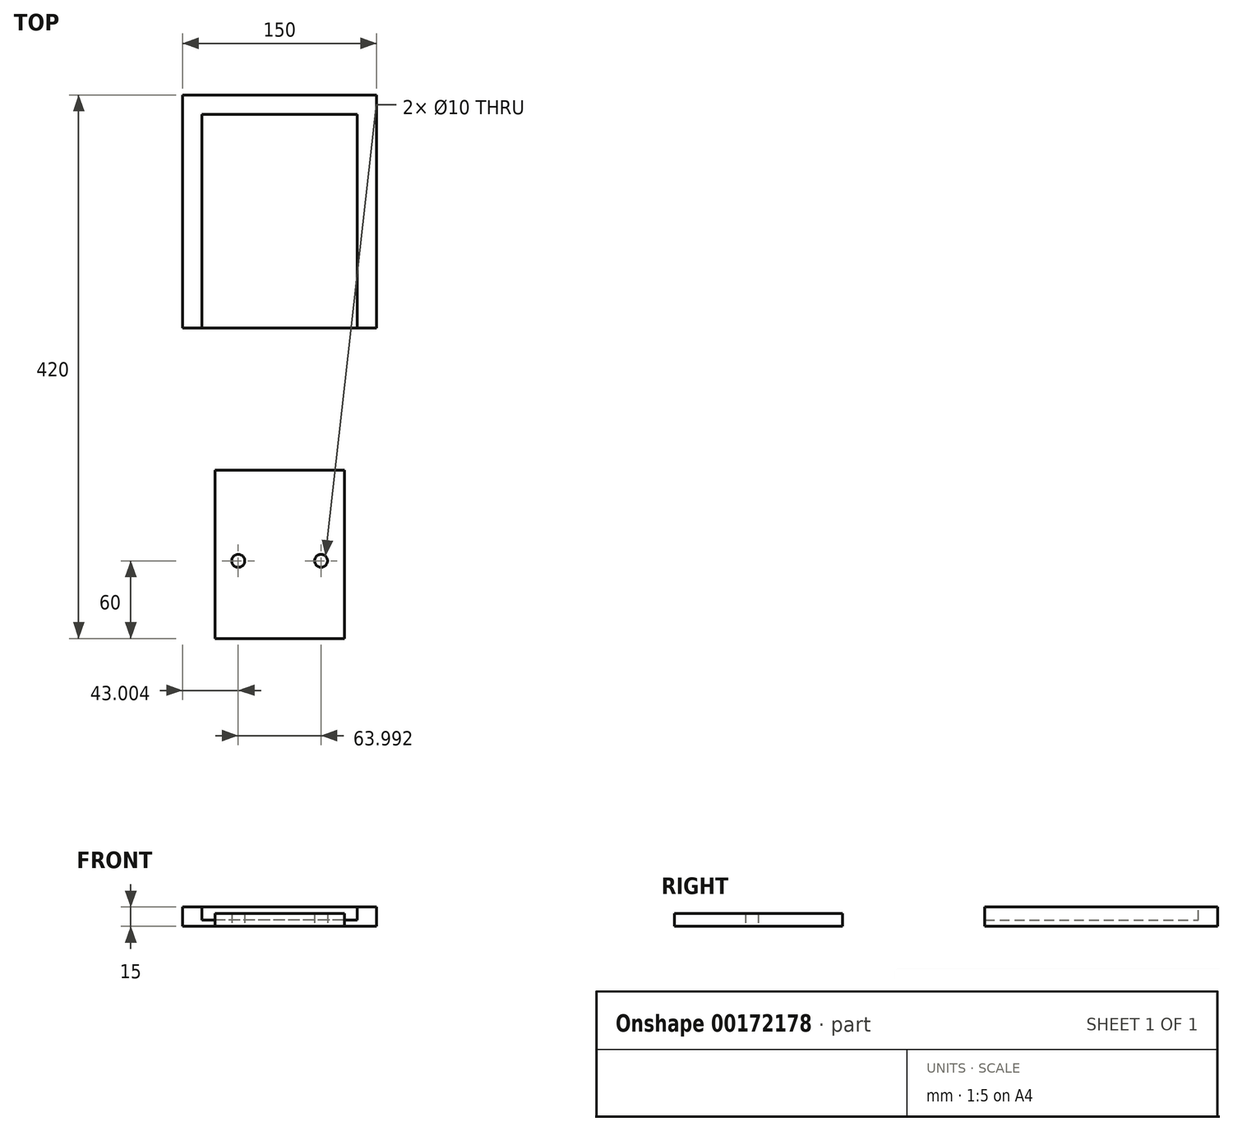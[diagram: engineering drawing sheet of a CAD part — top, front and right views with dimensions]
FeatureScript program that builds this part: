
annotation { "Feature Type Name" : "Feature", "Feature Type Description" : "" }
export const myFeature = defineFeature(function(context is Context, id is Id, definition is map)
    precondition{}
    {
        {
            var Q0;
            Q0=qCreatedBy(makeId("Top.planeOp"),FACE);
            var sketch = newSketch(context, id + "F0", { "sketchPlane" : qUnion([Q0])});
            skLineSegment(sketch, "E0.bottom", {"start": v(50, -90) * mm, "end": v(-50, -90) * mm});
            skLineSegment(sketch, "E0.top", {"start": v(50, 40) * mm, "end": v(-50, 40) * mm});
            skLineSegment(sketch, "E0.left", {"start": v(50, -90) * mm, "end": v(50, 40) * mm});
            skLineSegment(sketch, "E0.right", {"start": v(-50, -90) * mm, "end": v(-50, 40) * mm});
            skPoint(sketch, "E0.middle", {"position": v(0, -25) * mm});
            skSolve(sketch);
        }
        {
            var Q0;
            Q0 = qSketchRegion(id + "F0", true);
            extrude(context, id + "F1", {"entities" : qUnion([Q0]), "depth" : 10 * mm});
        }
        {
            var Q0;
            Q0=makeQuery(id+"F1.opExtrude","CAP_FACE",FACE,{"disambiguationData":[OSD([sQuery(id+"F0.wireOp",EDGE,"E0.bottom"),sQuery(id+"F0.wireOp",EDGE,"E0.top"),sQuery(id+"F0.wireOp",EDGE,"E0.left"),sQuery(id+"F0.wireOp",EDGE,"E0.right")])],"isStart":true});
            var sketch = newSketch(context, id + "F2", { "sketchPlane" : qUnion([Q0])});
            skCircle(sketch, "E1", {"center": v(32, 30) * mm, "radius": 5 * mm});
            skCircle(sketch, "E2", {"center": v(-32, 30) * mm, "radius": 5 * mm});
            skSolve(sketch);
        }
        {
            var Q0;
            Q0 = qSketchRegion(id + "F2", true);
            extrude(context, id + "F3", {"entities" : qUnion([Q0]), "operationType" : NewBodyOperationType.REMOVE, "oppositeDirection" : true, "depth" : 25 * mm});
        }
        {
            var Q0;
            Q0=qCreatedBy(makeId("Front.planeOp"),FACE);
            cPlane(context, id + "F4", {"entities" : qUnion([Q0]), "cplaneType" : CPlaneType.OFFSET, "offset" : 150 * mm, "oppositeDirection" : true, "width" : 150 * mm, "height" : 150 * mm});
        }
        {
            var Q0;
            Q0=qCreatedBy(makeId("Top.planeOp"),FACE);
            var sketch = newSketch(context, id + "F5", { "sketchPlane" : qUnion([Q0])});
            skLineSegment(sketch, "E3.bottom", {"start": v(75, 150) * mm, "end": v(-75, 150) * mm});
            skLineSegment(sketch, "E3.top", {"start": v(75, 330) * mm, "end": v(-75, 330) * mm});
            skLineSegment(sketch, "E3.left", {"start": v(75, 150) * mm, "end": v(75, 330) * mm});
            skLineSegment(sketch, "E3.right", {"start": v(-75, 150) * mm, "end": v(-75, 330) * mm});
            skPoint(sketch, "E3.middle", {"position": v(0, 240) * mm});
            skSolve(sketch);
        }
        {
            var Q0;
            Q0 = qSketchRegion(id + "F5", true);
            extrude(context, id + "F6", {"entities" : qUnion([Q0]), "depth" : 15 * mm});
        }
        {
            var Q0;
            Q0=makeQuery(id+"F6.opExtrude","CAP_FACE",FACE,{"disambiguationData":[OSD([sQuery(id+"F5.wireOp",EDGE,"E3.bottom"),sQuery(id+"F5.wireOp",EDGE,"E3.top"),sQuery(id+"F5.wireOp",EDGE,"E3.left"),sQuery(id+"F5.wireOp",EDGE,"E3.right")])],"isStart":false});
            var sketch = newSketch(context, id + "F7", { "sketchPlane" : qUnion([Q0])});
            skLineSegment(sketch, "E4.bottom", {"start": v(60, 150) * mm, "end": v(-60, 150) * mm});
            skLineSegment(sketch, "E4.top", {"start": v(60, 315) * mm, "end": v(-60, 315) * mm});
            skLineSegment(sketch, "E4.left", {"start": v(60, 150) * mm, "end": v(60, 315) * mm});
            skLineSegment(sketch, "E4.right", {"start": v(-60, 150) * mm, "end": v(-60, 315) * mm});
            skPoint(sketch, "E4.middle", {"position": v(0, 232.5) * mm});
            skSolve(sketch);
        }
        {
            var Q0;
            Q0 = qSketchRegion(id + "F7", true);
            extrude(context, id + "F8", {"entities" : qUnion([Q0]), "operationType" : NewBodyOperationType.REMOVE, "oppositeDirection" : true, "depth" : 10 * mm});
        }
    });
